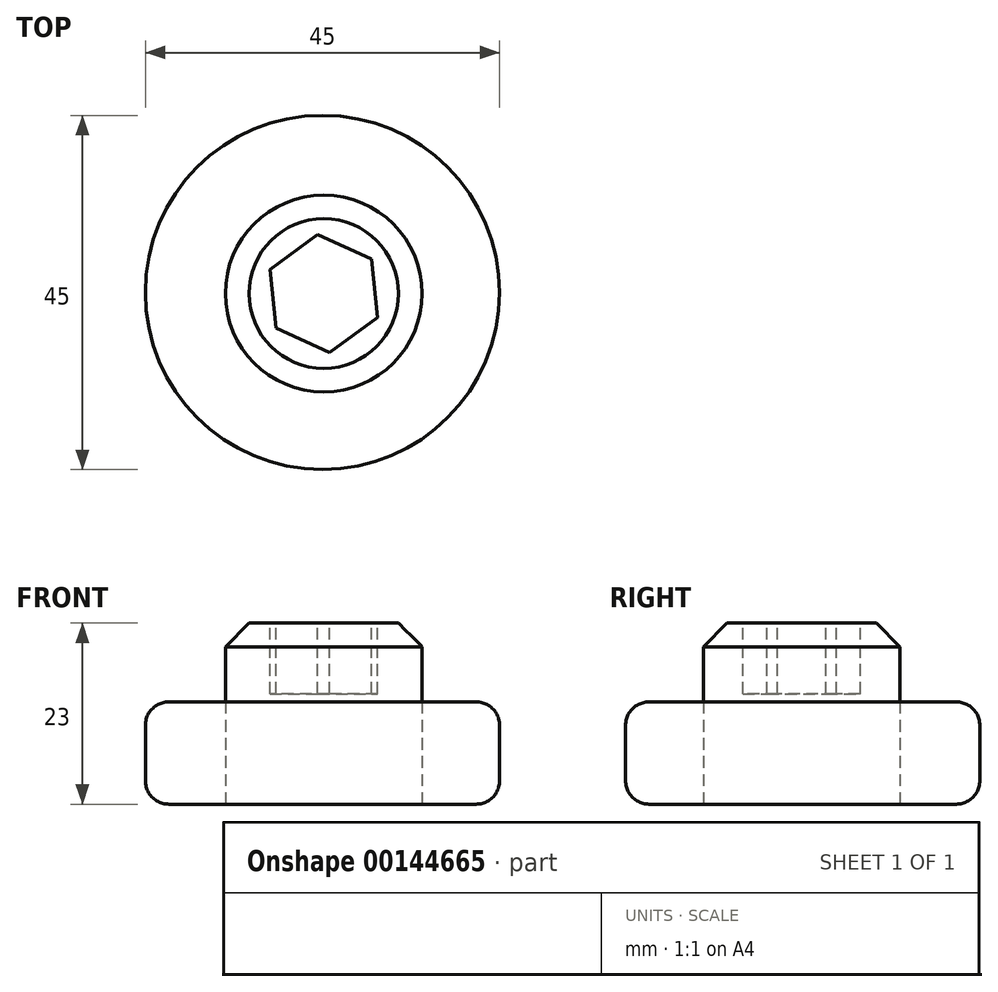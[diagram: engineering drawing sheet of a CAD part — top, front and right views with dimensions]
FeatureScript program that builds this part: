
annotation { "Feature Type Name" : "Feature", "Feature Type Description" : "" }
export const myFeature = defineFeature(function(context is Context, id is Id, definition is map)
    precondition{}
    {
        {
            var Q0;
            Q0=qCreatedBy(makeId("Top.planeOp"),FACE);
            var sketch = newSketch(context, id + "F0", { "sketchPlane" : qUnion([Q0])});
            skCircle(sketch, "E0", {"center": v(-37.33, 37.77) * mm, "radius": 22.5 * mm});
            skSolve(sketch);
        }
        {
            var Q0;
            Q0=qCreatedBy(makeId("Top.planeOp"),FACE);
            var sketch = newSketch(context, id + "F1", { "sketchPlane" : qUnion([Q0])});
            skCircle(sketch, "E1", {"center": v(-37.17, 37.64) * mm, "radius": 12.5 * mm});
            skSolve(sketch);
        }
        {
            var Q0;
            Q0=makeQuery(id+"F1.imprint","IMPRINT",FACE,{"disambiguationData":[TD([[makeQuery(id+"F1.imprint","IMPRINT",EDGE,{"derivedFrom":sQuery(id+"F1.wireOp",EDGE,"E1")}),1.0]])]});
            var Q1;
            Q1=makeQuery(id+"F0.imprint","IMPRINT",FACE,{"disambiguationData":[TD([[makeQuery(id+"F0.imprint","IMPRINT",EDGE,{"derivedFrom":sQuery(id+"F0.wireOp",EDGE,"E0")}),1.0]])]});
            extrude(context, id + "F2", {"entities" : qUnion([Q0, Q1]), "flatOperationType" : FlatOperationType.REMOVE, "offsetDistance" : 25 * mm, "depth" : 13 * mm, "domain" : OperationDomain.MODEL});
        }
        {
            var Q0;
            Q0=makeQuery(id+"F2.opExtrude","CAP_FACE",FACE,{"disambiguationData":[OSD([sQuery(id+"F1.wireOp",EDGE,"E1")])],"isStart":false});
            extrude(context, id + "F3", {"entities" : qUnion([Q0]), "depth" : 10 * mm});
        }
        {
            var Q0;
            Q0=makeQuery(id+"F3.opExtrude","CAP_FACE",FACE,{"disambiguationData":[OSD([sQuery(id+"F1.wireOp",EDGE,"E1")])],"isStart":false});
            var sketch = newSketch(context, id + "F4", { "sketchPlane" : qUnion([Q0])});
            skCircle(sketch, "E2.cCircle", {"center": v(-37.17, 37.64) * mm, "radius": 6.5 * mm, "construction": true});
            skLineSegment(sketch, "E2.0", {"start": v(-30.32, 34.57) * mm, "end": v(-36.4, 30.17) * mm});
            skLineSegment(sketch, "E2.1", {"start": v(-36.4, 30.17) * mm, "end": v(-43.25, 33.24) * mm});
            skLineSegment(sketch, "E2.2", {"start": v(-43.25, 33.24) * mm, "end": v(-44.02, 40.7) * mm});
            skLineSegment(sketch, "E2.3", {"start": v(-44.02, 40.7) * mm, "end": v(-37.94, 45.1) * mm});
            skLineSegment(sketch, "E2.4", {"start": v(-37.94, 45.1) * mm, "end": v(-31.09, 42.04) * mm});
            skLineSegment(sketch, "E2.5", {"start": v(-31.09, 42.04) * mm, "end": v(-30.32, 34.57) * mm});
            skPoint(sketch, "E2.0.midPoint", {"position": v(-33.36, 32.37) * mm});
            skSolve(sketch);
        }
        {
            var Q0;
            Q0=makeQuery(id+"F2.opExtrude","CAP_EDGE",EDGE,{"disambiguationData":[OSD([sQuery(id+"F0.wireOp",EDGE,"E0")])],"isStart":false});
            var Q1;
            Q1=makeQuery(id+"F2.opExtrude","CAP_EDGE",EDGE,{"disambiguationData":[OSD([sQuery(id+"F0.wireOp",EDGE,"E0")])],"isStart":true});
            fillet(context, id + "F5", {"entities" : qUnion([Q0, Q1]), "radius" : 3 * mm, "tangentPropagation" : true, "allowEdgeOverflow" : false});
        }
        {
            var Q0;
            Q0=makeQuery(id+"F3.opExtrude","CAP_EDGE",EDGE,{"disambiguationData":[OSD([sQuery(id+"F1.wireOp",EDGE,"E1")])],"isStart":false});
            chamfer(context, id + "F6", {"entities" : qUnion([Q0]), "width" : 3 * mm, "tangentPropagation" : true});
        }
        {
            var Q0;
            Q0=makeQuery(id+"F2.opExtrude","CAP_FACE",FACE,{"disambiguationData":[OSD([sQuery(id+"F0.wireOp",EDGE,"E0")])],"isStart":true});
            var sketch = newSketch(context, id + "F7", { "sketchPlane" : qUnion([Q0])});
            skCircle(sketch, "E3", {"center": v(-44.97, -24.12) * mm, "radius": 4 * mm});
            skSolve(sketch);
        }
        {
            var Q0;
            Q0=makeQuery(id+"F4.imprint","IMPRINT",FACE,{"disambiguationData":[TD([[makeQuery(id+"F4.imprint","IMPRINT",EDGE,{"derivedFrom":sQuery(id+"F4.wireOp",EDGE,"E2.0")}),-1.0]])]});
            extrude(context, id + "F8", {"entities" : qUnion([Q0]), "operationType" : NewBodyOperationType.REMOVE, "oppositeDirection" : true, "depth" : 9 * mm});
        }
        {
            var Q0;
            Q0=sQuery(id+"F7.wireOp",EDGE,"E3");
            extrude(context, id + "F9", {"bodyType" : ToolBodyType.SURFACE, "surfaceEntities" : qUnion([Q0]), "oppositeDirection" : true, "depth" : 14 * mm});
        }
    });
